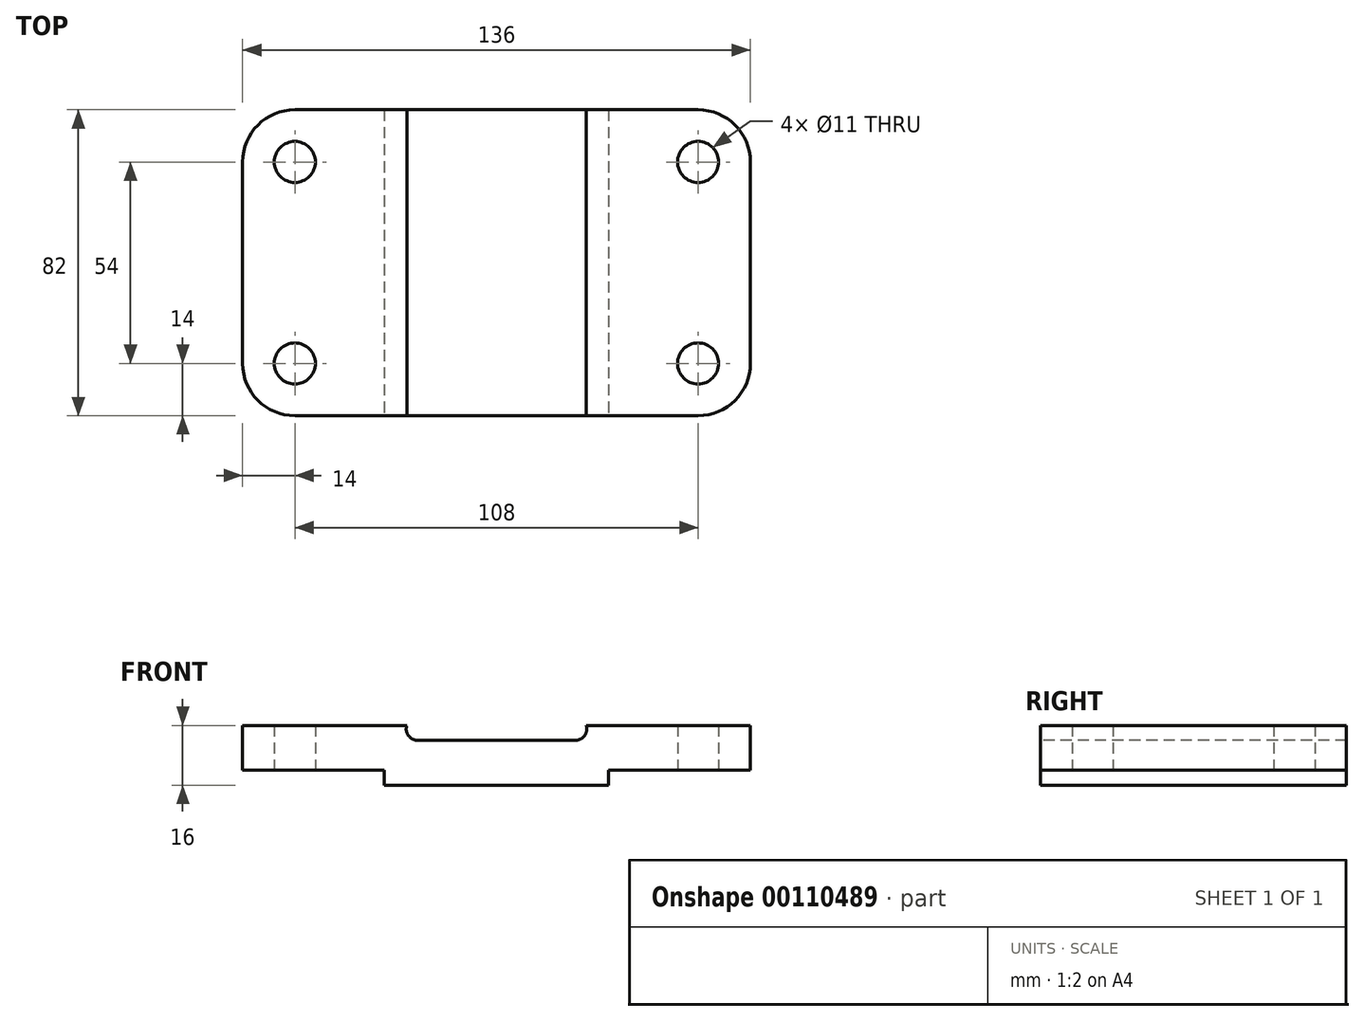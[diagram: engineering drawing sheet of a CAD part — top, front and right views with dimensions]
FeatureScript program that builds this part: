
annotation { "Feature Type Name" : "Feature", "Feature Type Description" : "" }
export const myFeature = defineFeature(function(context is Context, id is Id, definition is map)
    precondition{}
    {
        {
            var Q0;
            Q0=qCreatedBy(makeId("Top.planeOp"),FACE);
            var sketch = newSketch(context, id + "F0", { "sketchPlane" : qUnion([Q0])});
            skLineSegment(sketch, "E0.bottom", {"start": v(54, 41) * mm, "end": v(-54, 41) * mm});
            skLineSegment(sketch, "E0.top", {"start": v(54, -41) * mm, "end": v(-54, -41) * mm});
            skLineSegment(sketch, "E0.left", {"start": v(68, 27) * mm, "end": v(68, -27) * mm});
            skLineSegment(sketch, "E0.right", {"start": v(-68, 27) * mm, "end": v(-68, -27) * mm});
            skPoint(sketch, "E0.middle", {"position": v(0, 0) * mm});
            skPoint(sketch, "E1.visualSharp", {"position": v(-68, 41) * mm});
            skArc(sketch, "E1.filletArc", {"start": v(-54, 41) * mm, "mid": v(-63.9, 36.9) * mm, "end": v(-68, 27) * mm});
            skPoint(sketch, "E2.visualSharp", {"position": v(-68, -41) * mm});
            skArc(sketch, "E2.filletArc", {"start": v(-68, -27) * mm, "mid": v(-63.9, -36.9) * mm, "end": v(-54, -41) * mm});
            skPoint(sketch, "E3.visualSharp", {"position": v(68, -41) * mm});
            skArc(sketch, "E3.filletArc", {"start": v(54, -41) * mm, "mid": v(63.9, -36.9) * mm, "end": v(68, -27) * mm});
            skPoint(sketch, "E4.visualSharp", {"position": v(68, 41) * mm});
            skArc(sketch, "E4.filletArc", {"start": v(68, 27) * mm, "mid": v(63.9, 36.9) * mm, "end": v(54, 41) * mm});
            skLineSegment(sketch, "E5", {"start": v(-54, 41) * mm, "end": v(-54, -41) * mm, "construction": true});
            skLineSegment(sketch, "E6", {"start": v(54, 41) * mm, "end": v(54, -41) * mm, "construction": true});
            skLineSegment(sketch, "E7", {"start": v(-68, 27) * mm, "end": v(68, 27) * mm, "construction": true});
            skLineSegment(sketch, "E8", {"start": v(-68, -27) * mm, "end": v(68, -27) * mm, "construction": true});
            skCircle(sketch, "E9", {"center": v(-54, 27) * mm, "radius": 5.5 * mm});
            skCircle(sketch, "E10", {"center": v(54, 27) * mm, "radius": 5.5 * mm});
            skCircle(sketch, "E11", {"center": v(-54, -27) * mm, "radius": 5.5 * mm});
            skCircle(sketch, "E12", {"center": v(54, -27) * mm, "radius": 5.5 * mm});
            skLineSegment(sketch, "E13", {"start": v(-24, 41) * mm, "end": v(-24, -41) * mm});
            skLineSegment(sketch, "E14", {"start": v(24, -41) * mm, "end": v(24, 41) * mm});
            skSolve(sketch);
        }
        {
            var Q0;
            Q0 = qSketchRegion(id + "F0", true);
            extrude(context, id + "F1", {"entities" : qUnion([Q0]), "depth" : 16 * mm});
        }
        {
            var Q0;
            Q0=makeQuery(id+"F1.opExtrude","SWEPT_FACE",FACE,{"disambiguationData":[OSD([sQuery(id+"F0.wireOp",EDGE,"E0.top")])]});
            var sketch = newSketch(context, id + "F2", { "sketchPlane" : qUnion([Q0])});
            skLineSegment(sketch, "E15", {"start": v(-68, 16) * mm, "end": v(-24, 16) * mm});
            skLineSegment(sketch, "E16", {"start": v(-68, 16) * mm, "end": v(-68, 4) * mm});
            skLineSegment(sketch, "E17", {"start": v(-68, 4) * mm, "end": v(-30, 4) * mm});
            skLineSegment(sketch, "E18", {"start": v(-30, 4) * mm, "end": v(-30, 0) * mm});
            skLineSegment(sketch, "E19", {"start": v(-30, 0) * mm, "end": v(30, 0) * mm});
            skLineSegment(sketch, "E20", {"start": v(30, 0) * mm, "end": v(30, 4) * mm});
            skLineSegment(sketch, "E21", {"start": v(30, 4) * mm, "end": v(68, 4) * mm});
            skLineSegment(sketch, "E22", {"start": v(68, 4) * mm, "end": v(68, 16) * mm});
            skLineSegment(sketch, "E23", {"start": v(68, 16) * mm, "end": v(24, 16) * mm});
            skLineSegment(sketch, "E24", {"start": v(-21.17, 12) * mm, "end": v(21.17, 12) * mm});
            skArc(sketch, "E25", {"start": v(21.17, 12) * mm, "mid": v(23.62, 13.27) * mm, "end": v(24, 16) * mm});
            skArc(sketch, "E26", {"start": v(-21.17, 12) * mm, "mid": v(-23.62, 13.27) * mm, "end": v(-24, 16) * mm});
            skLineSegment(sketch, "E27", {"start": v(68, 4) * mm, "end": v(68, 0) * mm});
            skLineSegment(sketch, "E28", {"start": v(68, 0) * mm, "end": v(30, 0) * mm});
            skLineSegment(sketch, "E29", {"start": v(-68, 4) * mm, "end": v(-68, 0) * mm});
            skLineSegment(sketch, "E30", {"start": v(-68, 0) * mm, "end": v(-30, 0) * mm});
            skSolve(sketch);
        }
        {
            var Q0;
            {var subQ0=sQuery(id+"F2.wireOp",EDGE,"E29");Q0=makeQuery(id+"F2.imprint","IMPRINT",FACE,{"disambiguationData":[TD([[makeQuery(id+"F2.imprint","IMPRINT",EDGE,{"derivedFrom":subQ0}),1.0]])]});}
            var Q1;
            {var subQ0=sQuery(id+"F2.wireOp",EDGE,"E27");Q1=makeQuery(id+"F2.imprint","IMPRINT",FACE,{"disambiguationData":[TD([[makeQuery(id+"F2.imprint","IMPRINT",EDGE,{"derivedFrom":subQ0}),-1.0]])]});}
            var Q2;
            Q2=makeQuery(id+"F2.imprint","IMPRINT",FACE,{"disambiguationData":[TD([[makeQuery(id+"F2.imprint","IMPRINT",EDGE,{"derivedFrom":sQuery(id+"F2.wireOp",EDGE,"E24")}),1.0]])]});
            var Q3;
            {var subQ0=sQuery(id+"F2.wireOp",EDGE,"E18");Q3=makeQuery(id+"F2.imprint","IMPRINT",FACE,{"disambiguationData":[TD([[makeQuery(id+"F2.imprint","IMPRINT",EDGE,{"derivedFrom":subQ0}),-1.0]])]});}
            var Q4;
            {var subQ0=sQuery(id+"F2.wireOp",EDGE,"E20");Q4=makeQuery(id+"F2.imprint","IMPRINT",FACE,{"disambiguationData":[TD([[makeQuery(id+"F2.imprint","IMPRINT",EDGE,{"derivedFrom":subQ0}),-1.0]])]});}
            extrude(context, id + "F3", {"entities" : qUnion([Q0, Q1, Q2, Q3, Q4]), "operationType" : NewBodyOperationType.REMOVE, "endBound" : BoundingType.THROUGH_ALL, "oppositeDirection" : true, "depth" : 25 * mm});
        }
    });
